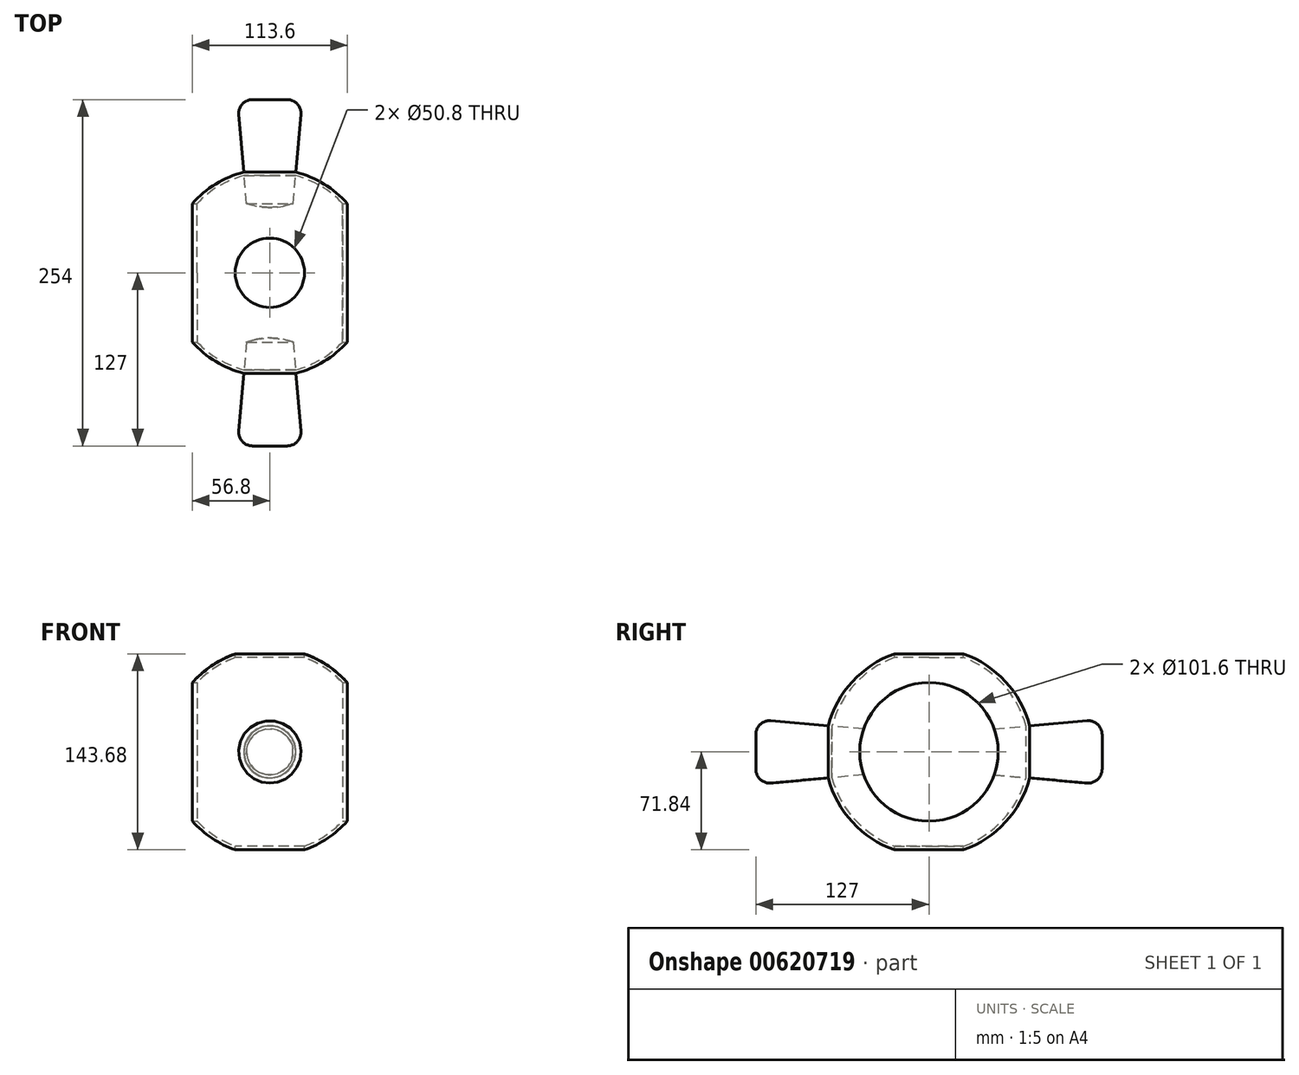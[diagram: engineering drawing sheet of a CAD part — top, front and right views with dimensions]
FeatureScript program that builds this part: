
annotation { "Feature Type Name" : "Feature", "Feature Type Description" : "" }
export const myFeature = defineFeature(function(context is Context, id is Id, definition is map)
    precondition{}
    {
        {
            var Q0;
            Q0=qCreatedBy(makeId("Top.planeOp"),FACE);
            var sketch = newSketch(context, id + "F0", { "sketchPlane" : qUnion([Q0])});
            skArc(sketch, "E0", {"start": v(76.2, 0) * mm, "mid": v(0, 76.2) * mm, "end": v(-76.2, 0) * mm});
            skLineSegment(sketch, "E1", {"start": v(-76.2, 0) * mm, "end": v(76.2, 0) * mm});
            skSolve(sketch);
        }
        {
            var Q0;
            Q0=makeQuery(id+"F0.imprint","IMPRINT",FACE,{"disambiguationData":[TD([[makeQuery(id+"F0.imprint","IMPRINT",EDGE,{"derivedFrom":sQuery(id+"F0.wireOp",EDGE,"E0")}),1.0]])]});
            var Q1;
            Q1=sQuery(id+"F0.wireOp",EDGE,"E1");
            revolve(context, id + "F1", {"surfaceOperationType" : NewSurfaceOperationType.NEW, "entities" : qUnion([Q0]), "axis" : qUnion([Q1]), "revolveType" : RevolveType.FULL});
        }
        {
            var Q0;
            Q0=qCreatedBy(makeId("Top.planeOp"),FACE);
            var sketch = newSketch(context, id + "F2", { "sketchPlane" : qUnion([Q0])});
            skCircle(sketch, "E2", {"center": v(0, 0) * mm, "radius": 25.4 * mm});
            skLineSegment(sketch, "E3", {"start": v(25.4, 0) * mm, "end": v(-25.4, 0) * mm});
            skSolve(sketch);
        }
        {
            var Q0;
            Q0=makeQuery(id+"F1.opRevolve","SWEPT_FACE",FACE,{"disambiguationData":[OSD([sQuery(id+"F0.wireOp",EDGE,"E0")])]});
            var Q1;
            Q1=makeQuery(id+"F1.opRevolve","SWEPT_BODY",BODY,{"disambiguationData":[OSD([sQuery(id+"F0.wireOp",EDGE,"E0"),sQuery(id+"F0.wireOp",EDGE,"E1")])]});
            shell(context, id + "F3", {"isHollow" : true, "entities" : qUnion([Q0]), "parts" : qUnion([Q1]), "thickness" : 2.54 * mm});
        }
        {
            var Q0;
            Q0 = qSketchRegion(id + "F2", true);
            extrude(context, id + "F4", {"entities" : qUnion([Q0]), "operationType" : NewBodyOperationType.REMOVE, "endBound" : BoundingType.SYMMETRIC, "oppositeDirection" : true, "depth" : 152.4 * mm, "offsetDistance" : 25.4 * mm});
        }
        {
            var Q0;
            {var subQ0=sQuery(id+"F2.wireOp",EDGE,"E3");Q0=makeQuery(id+"F2.imprint","IMPRINT",FACE,{"disambiguationData":[TD([[makeQuery(id+"F2.imprint","IMPRINT",EDGE,{"derivedFrom":subQ0}),-1.0]])]});}
            var Q1;
            Q1=sQuery(id+"F2.wireOp",EDGE,"E3");
            revolve(context, id + "F5", {"surfaceOperationType" : NewSurfaceOperationType.NEW, "entities" : qUnion([Q0]), "axis" : qUnion([Q1]), "revolveType" : RevolveType.FULL});
        }
        {
            var Q0;
            Q0=qCreatedBy(makeId("Top.planeOp"),FACE);
            var sketch = newSketch(context, id + "F6", { "sketchPlane" : qUnion([Q0])});
            skLineSegment(sketch, "E4", {"start": v(97, 0) * mm, "end": v(-100.96, 0) * mm});
            skSolve(sketch);
        }
        {
            var Q0;
            Q0=qCreatedBy(makeId("Front.planeOp"),FACE);
            var sketch = newSketch(context, id + "F7", { "sketchPlane" : qUnion([Q0])});
            skCircle(sketch, "E5", {"center": v(0, 0) * mm, "radius": 12.7 * mm});
            skSolve(sketch);
        }
        {
            var Q0;
            Q0 = qSketchRegion(id + "F7", true);
            extrude(context, id + "F8", {"entities" : qUnion([Q0]), "operationType" : NewBodyOperationType.ADD, "endBound" : BoundingType.SYMMETRIC, "depth" : 254 * mm, "offsetDistance" : 25.4 * mm, "hasDraft" : true, "draftAngle" : 5 * degree});
        }
        {
            var Q0;
            Q0=qCreatedBy(makeId("Right.planeOp"),FACE);
            var sketch = newSketch(context, id + "F9", { "sketchPlane" : qUnion([Q0])});
            skCircle(sketch, "E6", {"center": v(0, 0) * mm, "radius": 50.8 * mm});
            skSolve(sketch);
        }
        {
            var Q0;
            Q0 = qSketchRegion(id + "F9", true);
            extrude(context, id + "F10", {"entities" : qUnion([Q0]), "operationType" : NewBodyOperationType.REMOVE, "endBound" : BoundingType.SYMMETRIC, "oppositeDirection" : true, "depth" : 152.4 * mm, "offsetDistance" : 25.4 * mm});
        }
        {
            var Q0;
            Q0=makeQuery(id+"FKziWSuxoX7L7UT_2.1.F8.boolean.opBoolean","INTERSECT",EDGE,{"derivedFrom":[makeQuery(id+"F5.opRevolve","SWEPT_FACE",FACE,{"disambiguationData":[OSD([sQuery(id+"F2.wireOp",EDGE,"E2")])]}),makeQuery(id+"FKziWSuxoX7L7UT_2.1.F8.*.split.splitOp","SPLIT",FACE,{"derivedFrom":makeQuery(id+"FKziWSuxoX7L7UT_2.1.F8.opExtrude","SWEPT_FACE",FACE,{"disambiguationData":[OSD([sQuery(id+"F7.wireOp",EDGE,"E5")])]})})]});
            var Q1;
            Q1=makeQuery(id+"F8.boolean.opBoolean","INTERSECT",EDGE,{"derivedFrom":[makeQuery(id+"F5.opRevolve","SWEPT_FACE",FACE,{"disambiguationData":[OSD([sQuery(id+"F2.wireOp",EDGE,"E2")])]}),makeQuery(id+"F8.*.split.splitOp","SPLIT",FACE,{"derivedFrom":makeQuery(id+"F8.opExtrude","SWEPT_FACE",FACE,{"disambiguationData":[OSD([sQuery(id+"F7.wireOp",EDGE,"E5")])]})})]});
            var Q2;
            Q2=makeQuery(id+"FKziWSuxoX7L7UT_2.1.F8.boolean.opBoolean","INTERSECT",EDGE,{"derivedFrom":[makeQuery(id+"F5.opRevolve","SWEPT_FACE",FACE,{"disambiguationData":[OSD([sQuery(id+"F2.wireOp",EDGE,"E2")])]}),makeQuery(id+"FKziWSuxoX7L7UT_2.1.F8.*.split.splitOp","SPLIT",FACE,{"derivedFrom":makeQuery(id+"FKziWSuxoX7L7UT_2.1.F8.opExtrude","SWEPT_FACE",FACE,{"disambiguationData":[OSD([sQuery(id+"F7.wireOp",EDGE,"E5")])]}),"isFromBackBody":true})]});
            var Q3;
            Q3=makeQuery(id+"F8.boolean.opBoolean","INTERSECT",EDGE,{"derivedFrom":[makeQuery(id+"F5.opRevolve","SWEPT_FACE",FACE,{"disambiguationData":[OSD([sQuery(id+"F2.wireOp",EDGE,"E2")])]}),makeQuery(id+"F8.*.split.splitOp","SPLIT",FACE,{"derivedFrom":makeQuery(id+"F8.opExtrude","SWEPT_FACE",FACE,{"disambiguationData":[OSD([sQuery(id+"F7.wireOp",EDGE,"E5")])]}),"isFromBackBody":true})]});
            var Q4;
            Q4=makeQuery(id+"F8.opExtrude","CAP_FACE",FACE,{"disambiguationData":[OSD([sQuery(id+"F7.wireOp",EDGE,"E5")])],"isStart":true});
            var Q5;
            Q5=makeQuery(id+"FKziWSuxoX7L7UT_2.1.F8.opExtrude","CAP_EDGE",EDGE,{"disambiguationData":[OSD([sQuery(id+"F7.wireOp",EDGE,"E5")])],"isStart":false});
            var Q6;
            Q6=makeQuery(id+"F8.opExtrude","CAP_EDGE",EDGE,{"disambiguationData":[OSD([sQuery(id+"F7.wireOp",EDGE,"E5")])],"isStart":false});
            var Q7;
            Q7=makeQuery(id+"FKziWSuxoX7L7UT_2.1.F8.opExtrude","CAP_FACE",FACE,{"disambiguationData":[OSD([sQuery(id+"F7.wireOp",EDGE,"E5")])],"isStart":true});
            fillet(context, id + "F11", {"entities" : qUnion([Q0, Q1, Q2, Q3, Q4, Q5, Q6, Q7]), "radius" : 10.16 * mm, "tangentPropagation" : true, "allowEdgeOverflow" : false});
        }
    });
